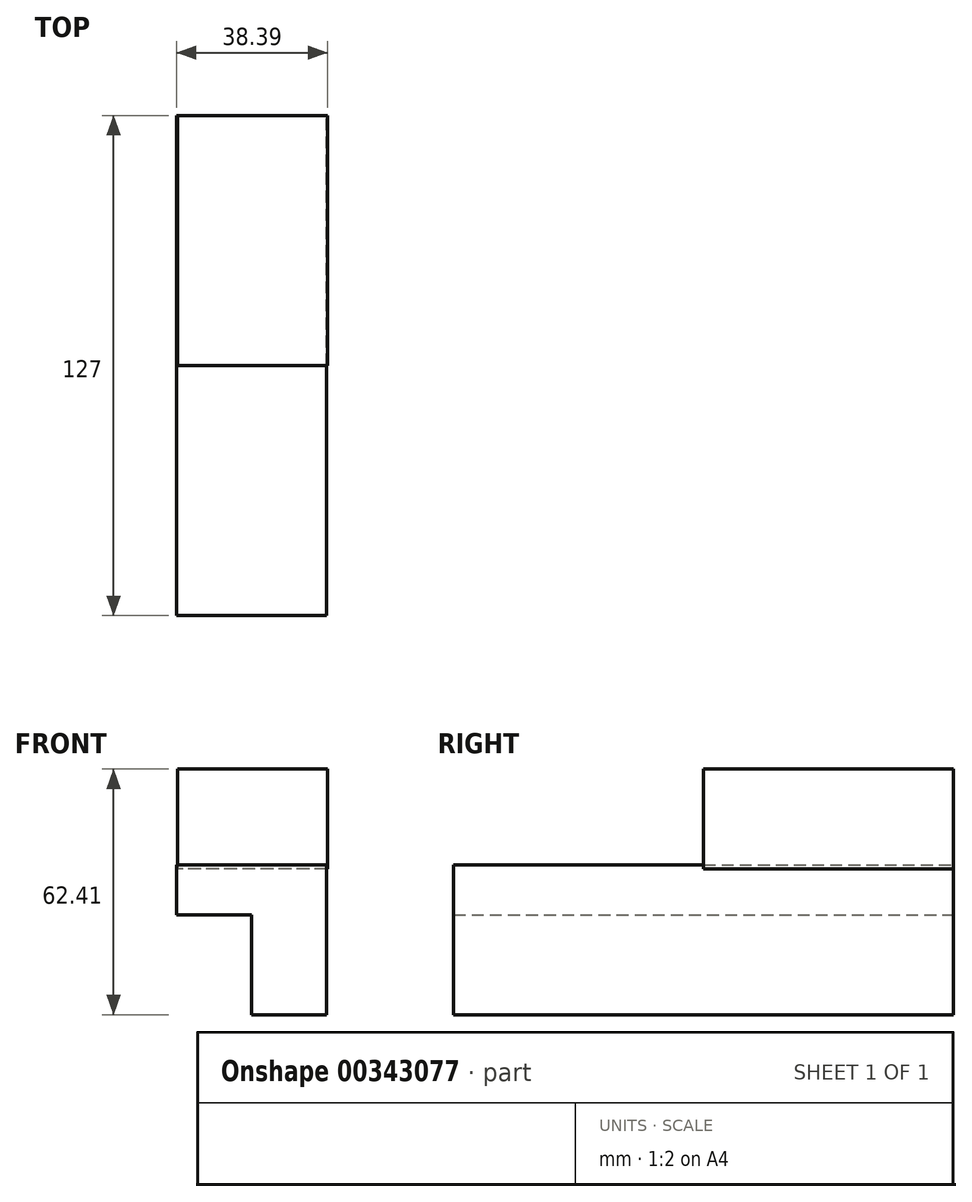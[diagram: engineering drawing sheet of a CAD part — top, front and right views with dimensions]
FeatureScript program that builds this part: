
annotation { "Feature Type Name" : "Feature", "Feature Type Description" : "" }
export const myFeature = defineFeature(function(context is Context, id is Id, definition is map)
    precondition{}
    {
        {
            var Q0;
            Q0=qCreatedBy(makeId("Front.planeOp"),FACE);
            var sketch = newSketch(context, id + "F0", { "sketchPlane" : qUnion([Q0])});
            skLineSegment(sketch, "E0", {"start": v(22.26, -47.07) * mm, "end": v(41.3, -47.07) * mm});
            skLineSegment(sketch, "E1", {"start": v(22.26, -47.07) * mm, "end": v(22.26, -21.67) * mm});
            skLineSegment(sketch, "E2", {"start": v(22.26, -21.67) * mm, "end": v(3.2, -21.67) * mm});
            skLineSegment(sketch, "E3", {"start": v(3.2, -21.67) * mm, "end": v(3.2, -8.97) * mm});
            skLineSegment(sketch, "E4", {"start": v(3.2, -8.97) * mm, "end": v(41.3, -8.97) * mm});
            skLineSegment(sketch, "E5", {"start": v(41.3, -8.97) * mm, "end": v(41.3, -47.07) * mm});
            skSolve(sketch);
        }
        {
            var Q0;
            Q0 = qSketchRegion(id + "F0", true);
            extrude(context, id + "F1", {"entities" : qUnion([Q0]), "depth" : 127 * mm});
        }
        {
            var Q0;
            Q0=qCreatedBy(makeId("Front.planeOp"),FACE);
            var sketch = newSketch(context, id + "F2", { "sketchPlane" : qUnion([Q0])});
            skLineSegment(sketch, "E6", {"start": v(41.6, -10.06) * mm, "end": v(41.6, 15.34) * mm});
            skLineSegment(sketch, "E7", {"start": v(41.6, 15.34) * mm, "end": v(3.5, 15.34) * mm});
            skLineSegment(sketch, "E8", {"start": v(3.5, 15.34) * mm, "end": v(3.5, -10.06) * mm});
            skLineSegment(sketch, "E9", {"start": v(41.6, -10.06) * mm, "end": v(3.5, -10.06) * mm});
            skSolve(sketch);
        }
        {
            var Q0;
            Q0 = qSketchRegion(id + "F2", true);
            extrude(context, id + "F3", {"entities" : qUnion([Q0]), "depth" : 63.5 * mm});
        }
        {
            var Q0;
            Q0 = qSketchRegion(id + "F2", true);
            extrude(context, id + "F4", {"entities" : qUnion([Q0]), "depth" : 63.5 * mm});
        }
    });
